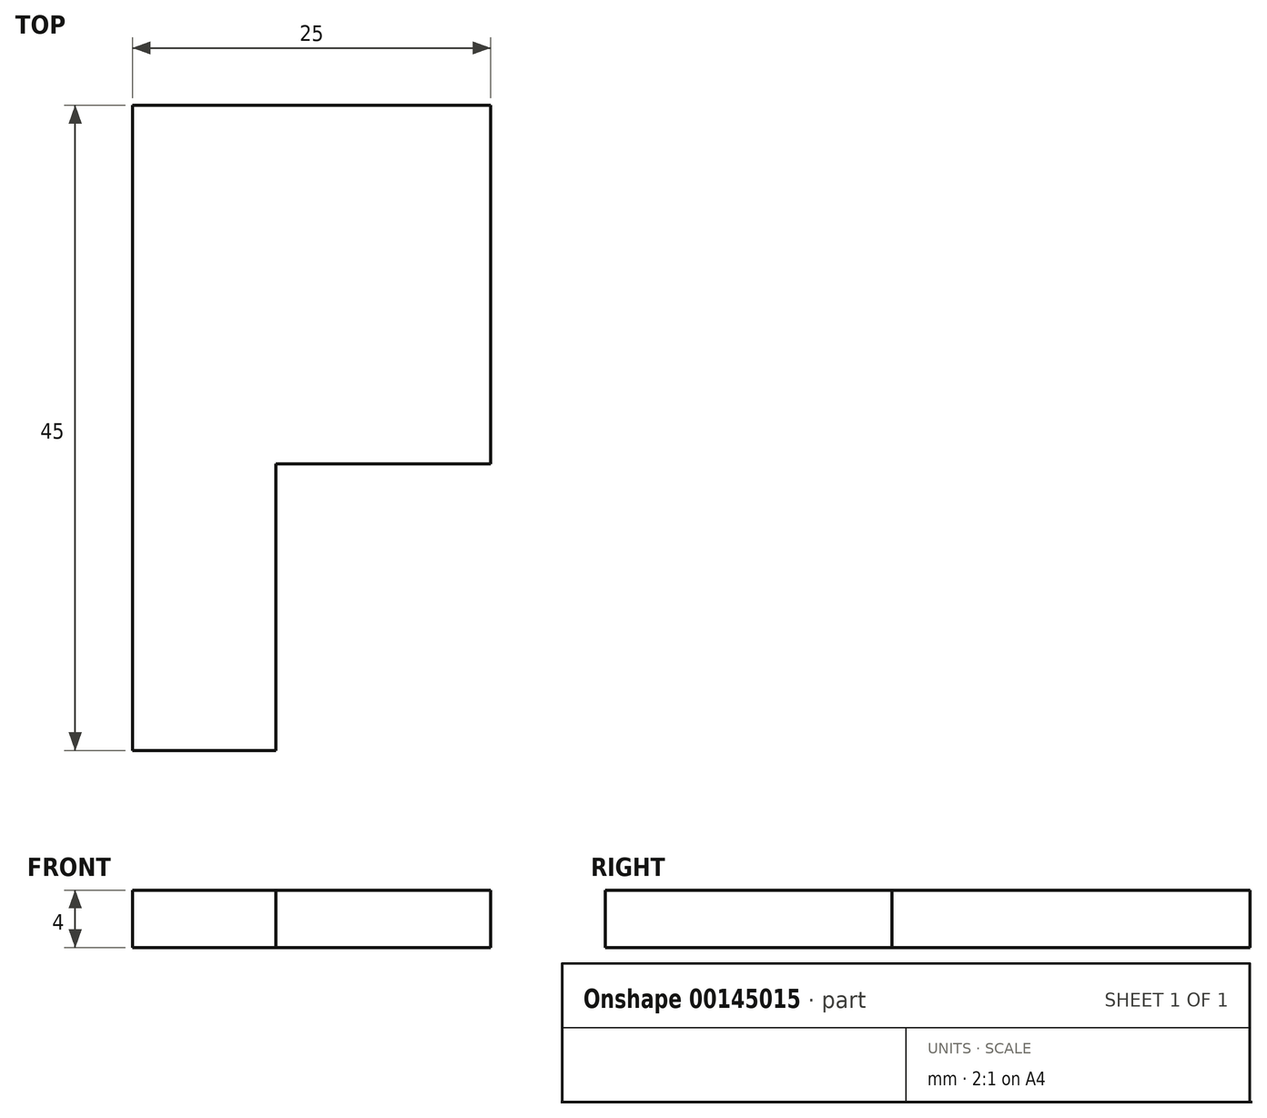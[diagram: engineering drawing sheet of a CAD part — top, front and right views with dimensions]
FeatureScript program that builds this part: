
annotation { "Feature Type Name" : "Feature", "Feature Type Description" : "" }
export const myFeature = defineFeature(function(context is Context, id is Id, definition is map)
    precondition{}
    {
        {
            var Q0;
            Q0=qCreatedBy(makeId("Top.planeOp"),FACE);
            var sketch = newSketch(context, id + "F0", { "sketchPlane" : qUnion([Q0])});
            skLineSegment(sketch, "E0.bottom", {"start": v(0, 0) * mm, "end": v(25, 0) * mm});
            skLineSegment(sketch, "E0.top", {"start": v(0, 25) * mm, "end": v(25, 25) * mm});
            skLineSegment(sketch, "E0.left", {"start": v(0, 0) * mm, "end": v(0, 25) * mm});
            skLineSegment(sketch, "E0.right", {"start": v(25, 0) * mm, "end": v(25, 25) * mm});
            skLineSegment(sketch, "E1.bottom", {"start": v(0, 0) * mm, "end": v(10, 0) * mm});
            skLineSegment(sketch, "E1.top", {"start": v(0, -20) * mm, "end": v(10, -20) * mm});
            skLineSegment(sketch, "E1.left", {"start": v(0, 0) * mm, "end": v(0, -20) * mm});
            skLineSegment(sketch, "E1.right", {"start": v(10, 0) * mm, "end": v(10, -20) * mm});
            skSolve(sketch);
        }
        {
            var Q0;
            Q0 = qSketchRegion(id + "F0", true);
            extrude(context, id + "F1", {"entities" : qUnion([Q0]), "depth" : 4 * mm});
        }
    });
